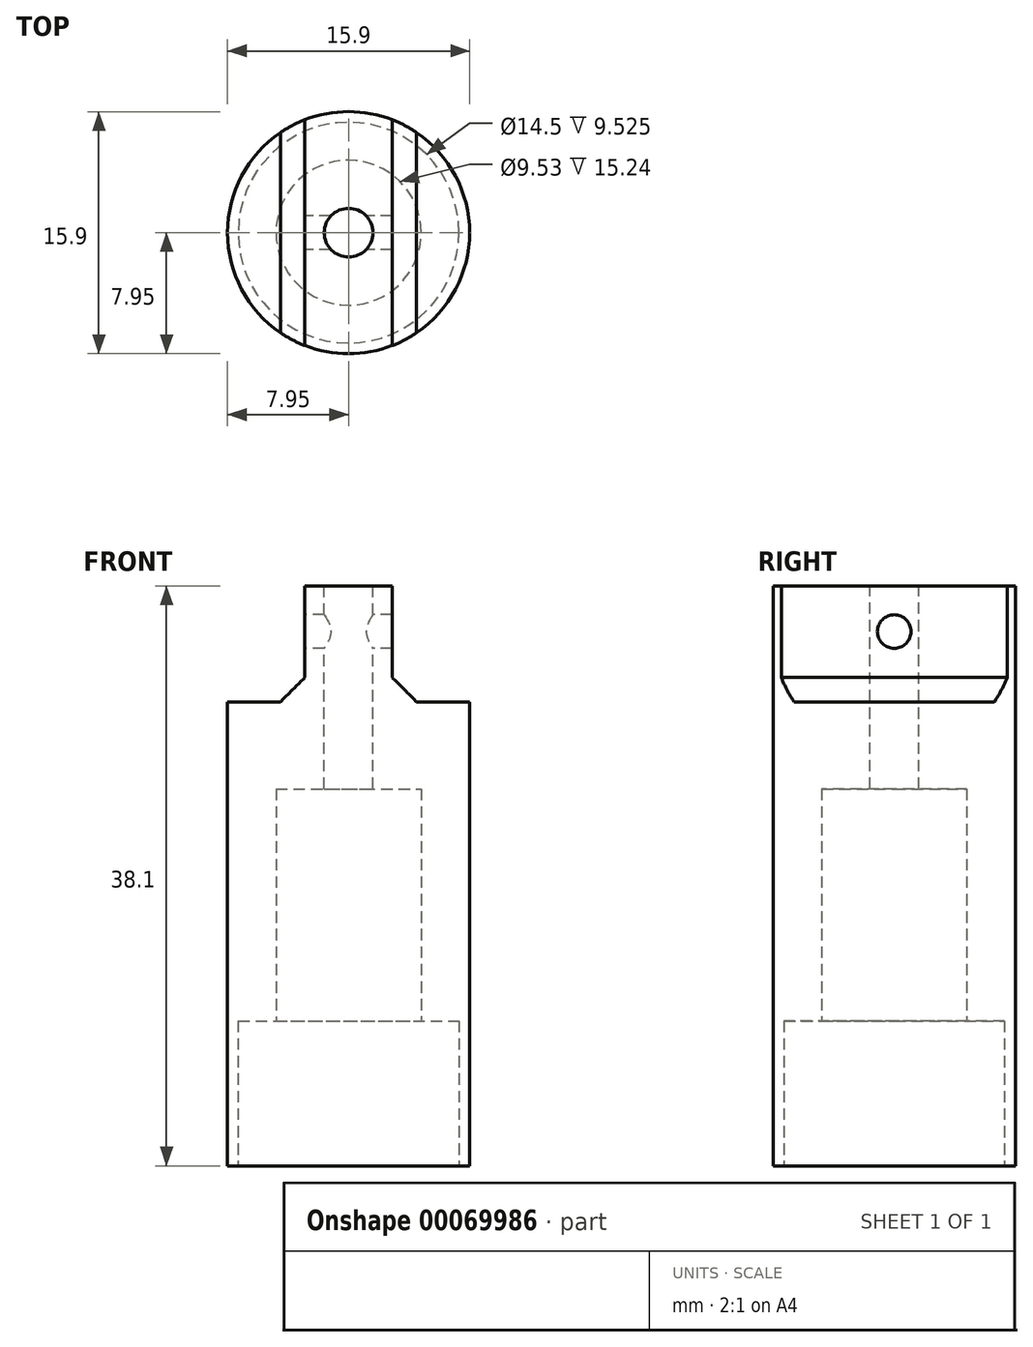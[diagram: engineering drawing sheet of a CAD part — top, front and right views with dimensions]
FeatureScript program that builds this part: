
annotation { "Feature Type Name" : "Feature", "Feature Type Description" : "" }
export const myFeature = defineFeature(function(context is Context, id is Id, definition is map)
    precondition{}
    {
        {
            var Q0;
            Q0=qCreatedBy(makeId("Top.planeOp"),FACE);
            var sketch = newSketch(context, id + "F0", { "sketchPlane" : qUnion([Q0])});
            skCircle(sketch, "E0", {"center": v(0, 0) * mm, "radius": 7.95 * mm});
            skSolve(sketch);
        }
        {
            var Q0;
            Q0 = qSketchRegion(id + "F0", true);
            extrude(context, id + "F1", {"entities" : qUnion([Q0]), "depth" : 38.1 * mm});
        }
        {
            var Q0;
            Q0=makeQuery(id+"F1.opExtrude","CAP_FACE",FACE,{"disambiguationData":[OSD([sQuery(id+"F0.wireOp",EDGE,"E0")])],"isStart":true});
            var sketch = newSketch(context, id + "F2", { "sketchPlane" : qUnion([Q0])});
            skCircle(sketch, "E1", {"center": v(0, 0) * mm, "radius": 7.25 * mm});
            skSolve(sketch);
        }
        {
            var Q0;
            Q0 = qSketchRegion(id + "F2", true);
            extrude(context, id + "F3", {"entities" : qUnion([Q0]), "operationType" : NewBodyOperationType.REMOVE, "oppositeDirection" : true, "depth" : 9.52 * mm});
        }
        {
            var Q0;
            Q0=makeQuery(id+"F3.boolean.opBoolean","COPY",FACE,{"derivedFrom":makeQuery(id+"F3.opExtrude","CAP_FACE",FACE,{"disambiguationData":[OSD([sQuery(id+"F2.wireOp",EDGE,"E1")])],"isStart":false})});
            var sketch = newSketch(context, id + "F4", { "sketchPlane" : qUnion([Q0])});
            skCircle(sketch, "E2", {"center": v(0, 0) * mm, "radius": 4.76 * mm});
            skSolve(sketch);
        }
        {
            var Q0;
            Q0 = qSketchRegion(id + "F4", true);
            extrude(context, id + "F5", {"entities" : qUnion([Q0]), "operationType" : NewBodyOperationType.REMOVE, "oppositeDirection" : true, "depth" : 15.24 * mm});
        }
        {
            var Q0;
            Q0=makeQuery(id+"F1.opExtrude","CAP_FACE",FACE,{"disambiguationData":[OSD([sQuery(id+"F0.wireOp",EDGE,"E0")])],"isStart":false});
            var sketch = newSketch(context, id + "F6", { "sketchPlane" : qUnion([Q0])});
            skCircle(sketch, "E3", {"center": v(0, 0) * mm, "radius": 1.6 * mm});
            skSolve(sketch);
        }
        {
            var Q0;
            Q0 = qSketchRegion(id + "F6", true);
            extrude(context, id + "F7", {"entities" : qUnion([Q0]), "operationType" : NewBodyOperationType.REMOVE, "oppositeDirection" : true, "depth" : 25.4 * mm});
        }
        {
            var Q0;
            Q0=makeQuery(id+"F1.opExtrude","CAP_FACE",FACE,{"disambiguationData":[OSD([sQuery(id+"F0.wireOp",EDGE,"E0")])],"isStart":false});
            var sketch = newSketch(context, id + "F8", { "sketchPlane" : qUnion([Q0])});
            skLineSegment(sketch, "E4.bottom", {"start": v(-2.87, 7.41) * mm, "end": v(-7.95, 7.41) * mm});
            skLineSegment(sketch, "E4.top", {"start": v(-2.87, -7.41) * mm, "end": v(-7.95, -7.41) * mm});
            skLineSegment(sketch, "E4.left", {"start": v(-2.87, 7.41) * mm, "end": v(-2.87, -7.41) * mm});
            skLineSegment(sketch, "E4.right", {"start": v(-7.95, 7.41) * mm, "end": v(-7.95, -7.41) * mm});
            skLineSegment(sketch, "E5.MirrorCS", {"start": v(7.95, 7.41) * mm, "end": v(7.95, -7.41) * mm});
            skLineSegment(sketch, "E6.MirrorCS", {"start": v(2.87, 7.41) * mm, "end": v(2.87, -7.41) * mm});
            skLineSegment(sketch, "E7.MirrorCS", {"start": v(2.87, -7.41) * mm, "end": v(7.95, -7.41) * mm});
            skLineSegment(sketch, "E8.MirrorCS", {"start": v(2.87, 7.41) * mm, "end": v(7.95, 7.41) * mm});
            skSolve(sketch);
        }
        {
            var Q0;
            Q0 = qSketchRegion(id + "F8", true);
            extrude(context, id + "F9", {"entities" : qUnion([Q0]), "operationType" : NewBodyOperationType.REMOVE, "oppositeDirection" : true, "depth" : 7.62 * mm});
        }
        {
            var Q0;
            Q0=makeQuery(id+"F9.boolean.opBoolean","COPY",FACE,{"derivedFrom":makeQuery(id+"F9.opExtrude","SWEPT_FACE",FACE,{"disambiguationData":[OSD([sQuery(id+"F8.wireOp",EDGE,"E4.left")])]})});
            var sketch = newSketch(context, id + "F10", { "sketchPlane" : qUnion([Q0])});
            skCircle(sketch, "E9", {"center": v(0, 35.1) * mm, "radius": 1.1 * mm});
            skSolve(sketch);
        }
        {
            var Q0;
            Q0 = qSketchRegion(id + "F10", true);
            extrude(context, id + "F11", {"entities" : qUnion([Q0]), "operationType" : NewBodyOperationType.REMOVE, "oppositeDirection" : true, "depth" : 25.4 * mm});
        }
        {
            var Q0;
            Q0=makeQuery(id+"F9.boolean.opBoolean","COPY",EDGE,{"derivedFrom":makeQuery(id+"F9.opExtrude","CAP_EDGE",EDGE,{"disambiguationData":[OSD([sQuery(id+"F8.wireOp",EDGE,"E4.left")])],"isStart":false})});
            var Q1;
            Q1=makeQuery(id+"F9.boolean.opBoolean","COPY",EDGE,{"derivedFrom":makeQuery(id+"F9.opExtrude","CAP_EDGE",EDGE,{"disambiguationData":[OSD([sQuery(id+"F8.wireOp",EDGE,"E6.MirrorCS")])],"isStart":false})});
            chamfer(context, id + "F12", {"entities" : qUnion([Q0, Q1]), "width" : 1.6 * mm, "tangentPropagation" : true});
        }
    });
